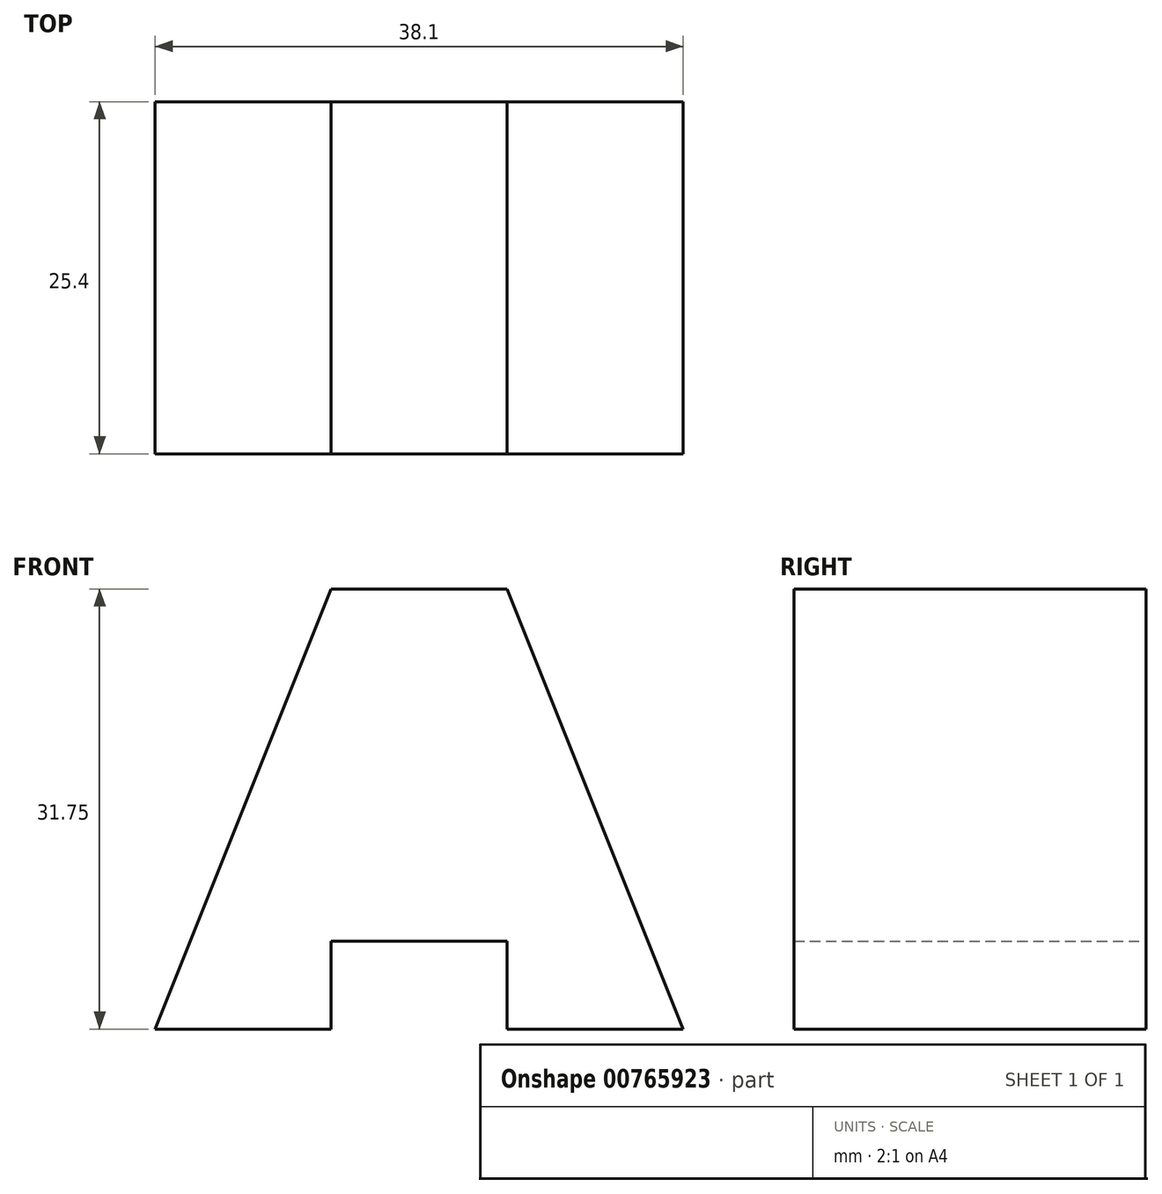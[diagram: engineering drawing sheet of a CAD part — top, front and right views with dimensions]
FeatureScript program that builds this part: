
annotation { "Feature Type Name" : "Feature", "Feature Type Description" : "" }
export const myFeature = defineFeature(function(context is Context, id is Id, definition is map)
    precondition{}
    {
        {
            var Q0;
            Q0=qCreatedBy(makeId("Front.planeOp"),FACE);
            var sketch = newSketch(context, id + "F0", { "sketchPlane" : qUnion([Q0])});
            skLineSegment(sketch, "E0", {"start": v(0, 31.75) * mm, "end": v(6.35, 31.75) * mm});
            skLineSegment(sketch, "E1", {"start": v(0, 31.75) * mm, "end": v(-6.35, 31.75) * mm});
            skLineSegment(sketch, "E2", {"start": v(-6.35, 31.75) * mm, "end": v(-19.05, 0) * mm});
            skLineSegment(sketch, "E3", {"start": v(6.35, 31.75) * mm, "end": v(19.05, 0) * mm});
            skLineSegment(sketch, "E4", {"start": v(-6.35, 0) * mm, "end": v(-6.35, 6.35) * mm});
            skLineSegment(sketch, "E5", {"start": v(-6.35, 6.35) * mm, "end": v(6.35, 6.35) * mm});
            skLineSegment(sketch, "E6", {"start": v(-6.35, 0) * mm, "end": v(-19.05, 0) * mm});
            skLineSegment(sketch, "E7", {"start": v(6.35, 6.35) * mm, "end": v(6.35, 0) * mm});
            skLineSegment(sketch, "E8", {"start": v(19.05, 0) * mm, "end": v(6.35, 0) * mm});
            skSolve(sketch);
        }
        {
            var Q0;
            Q0 = qSketchRegion(id + "F0", true);
            extrude(context, id + "F1", {"entities" : qUnion([Q0]), "depth" : 25.4 * mm, "offsetDistance" : 25.4 * mm});
        }
    });
